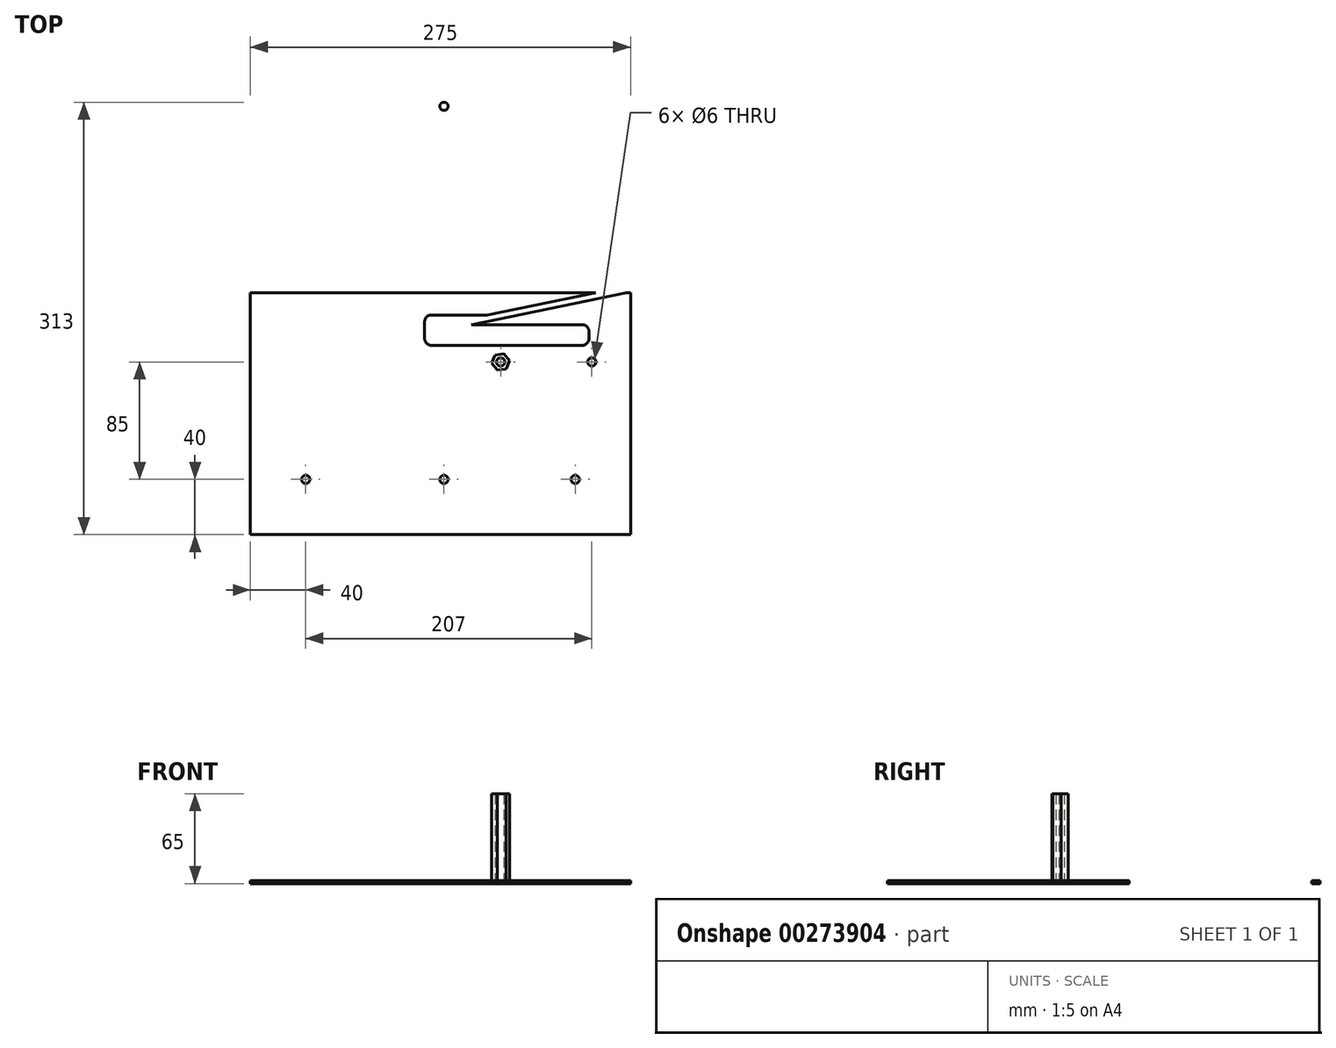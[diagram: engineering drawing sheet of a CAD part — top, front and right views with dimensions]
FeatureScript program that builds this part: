
annotation { "Feature Type Name" : "Feature", "Feature Type Description" : "" }
export const myFeature = defineFeature(function(context is Context, id is Id, definition is map)
    precondition{}
    {
        {
            var Q0;
            Q0=qCreatedBy(makeId("Top.planeOp"),FACE);
            var sketch = newSketch(context, id + "F0", { "sketchPlane" : qUnion([Q0])});
            skLineSegment(sketch, "E0.bottom", {"start": v(0, 0) * mm, "end": v(-275, 0) * mm});
            skLineSegment(sketch, "E0.top", {"start": v(-3, 175) * mm, "end": v(-275, 175) * mm});
            skLineSegment(sketch, "E0.left", {"start": v(0, 0) * mm, "end": v(0, 177) * mm});
            skLineSegment(sketch, "E0.right", {"start": v(-275, 0) * mm, "end": v(-275, 175) * mm});
            skLineSegment(sketch, "E1", {"start": v(-115, 152) * mm, "end": v(-35, 152) * mm});
            skLineSegment(sketch, "E2", {"start": v(-30, 147) * mm, "end": v(-30, 142) * mm});
            skLineSegment(sketch, "E3", {"start": v(-35, 137) * mm, "end": v(-144, 137) * mm});
            skLineSegment(sketch, "E4", {"start": v(-149, 142) * mm, "end": v(-149, 154) * mm});
            skLineSegment(sketch, "E5", {"start": v(-144, 159) * mm, "end": v(-104, 159) * mm});
            skLineSegment(sketch, "E6", {"start": v(-104, 159) * mm, "end": v(-25.36, 175) * mm});
            skCircle(sketch, "E7", {"center": v(-28, 125) * mm, "radius": 3 * mm});
            skCircle(sketch, "E8", {"center": v(-94, 125) * mm, "radius": 3 * mm});
            skPoint(sketch, "E9.visualSharp", {"position": v(0, 175) * mm});
            skLineSegment(sketch, "E10", {"start": v(-3, 175) * mm, "end": v(-115, 152) * mm});
            skLineSegment(sketch, "E11", {"start": v(-275, 40) * mm, "end": v(0, 40) * mm, "construction": true});
            skCircle(sketch, "E12", {"center": v(-235, 40) * mm, "radius": 3 * mm});
            skCircle(sketch, "E13", {"center": v(-135, 40) * mm, "radius": 3 * mm});
            skCircle(sketch, "E14", {"center": v(-40, 40) * mm, "radius": 3 * mm});
            skCircle(sketch, "E15.MirrorC", {"center": v(-135, 310) * mm, "radius": 3 * mm});
            skCircle(sketch, "E16.MirrorC", {"center": v(-94, 225) * mm, "radius": 3 * mm});
            skCircle(sketch, "E17.MirrorC", {"center": v(-40, 310) * mm, "radius": 3 * mm});
            skCircle(sketch, "E18.MirrorC", {"center": v(-28, 225) * mm, "radius": 3 * mm});
            skCircle(sketch, "E19.MirrorC", {"center": v(-235, 310) * mm, "radius": 3 * mm});
            skLineSegment(sketch, "E20.MirrorCS", {"start": v(-149, 208) * mm, "end": v(-149, 196) * mm});
            skLineSegment(sketch, "E21.MirrorCS", {"start": v(-144, 191) * mm, "end": v(-104, 191) * mm});
            skLineSegment(sketch, "E22.MirrorCS", {"start": v(-104, 191) * mm, "end": v(-25.36, 175) * mm});
            skLineSegment(sketch, "E23.MirrorCS", {"start": v(-35, 213) * mm, "end": v(-144, 213) * mm});
            skLineSegment(sketch, "E24.MirrorCS", {"start": v(-30, 203) * mm, "end": v(-30, 208) * mm});
            skLineSegment(sketch, "E25.MirrorCS", {"start": v(-115, 198) * mm, "end": v(-35, 198) * mm});
            skLineSegment(sketch, "E26.MirrorCS", {"start": v(-275, 350) * mm, "end": v(-275, 175) * mm});
            skLineSegment(sketch, "E27.MirrorCS", {"start": v(-3, 175) * mm, "end": v(-115, 198) * mm});
            skLineSegment(sketch, "E28.MirrorCS", {"start": v(0, 350) * mm, "end": v(0, 173) * mm});
            skLineSegment(sketch, "E29.MirrorCS", {"start": v(-275, 310) * mm, "end": v(0, 310) * mm, "construction": true});
            skLineSegment(sketch, "E30.MirrorCS", {"start": v(0, 350) * mm, "end": v(-275, 350) * mm});
            skCircle(sketch, "E31.cCircle", {"center": v(-94, 125) * mm, "radius": 5.57 * mm, "construction": true});
            skLineSegment(sketch, "E31.0", {"start": v(-91.54, 130.94) * mm, "end": v(-87.63, 125.85) * mm});
            skLineSegment(sketch, "E31.1", {"start": v(-87.63, 125.85) * mm, "end": v(-90.08, 119.9) * mm});
            skLineSegment(sketch, "E31.2", {"start": v(-90.08, 119.9) * mm, "end": v(-96.46, 119.06) * mm});
            skLineSegment(sketch, "E31.3", {"start": v(-96.46, 119.06) * mm, "end": v(-100.37, 124.15) * mm});
            skLineSegment(sketch, "E31.4", {"start": v(-100.37, 124.15) * mm, "end": v(-97.92, 130.1) * mm});
            skLineSegment(sketch, "E31.5", {"start": v(-97.92, 130.1) * mm, "end": v(-91.54, 130.94) * mm});
            skPoint(sketch, "E31.0.midPoint", {"position": v(-89.59, 128.4) * mm});
            skPoint(sketch, "E32.visualSharp", {"position": v(-149, 159) * mm});
            skArc(sketch, "E32.filletArc", {"start": v(-144, 159) * mm, "mid": v(-147.54, 157.54) * mm, "end": v(-149, 154) * mm});
            skPoint(sketch, "E33.visualSharp", {"position": v(-149, 137) * mm});
            skArc(sketch, "E33.filletArc", {"start": v(-149, 142) * mm, "mid": v(-147.54, 138.46) * mm, "end": v(-144, 137) * mm});
            skPoint(sketch, "E34.visualSharp", {"position": v(-30, 137) * mm});
            skArc(sketch, "E34.filletArc", {"start": v(-35, 137) * mm, "mid": v(-31.46, 138.46) * mm, "end": v(-30, 142) * mm});
            skPoint(sketch, "E35.visualSharp", {"position": v(-30, 152) * mm});
            skArc(sketch, "E35.filletArc", {"start": v(-30, 147) * mm, "mid": v(-31.46, 150.54) * mm, "end": v(-35, 152) * mm});
            skPoint(sketch, "E36.visualSharp", {"position": v(-149, 213) * mm});
            skArc(sketch, "E36.filletArc", {"start": v(-144, 213) * mm, "mid": v(-147.54, 211.54) * mm, "end": v(-149, 208) * mm});
            skPoint(sketch, "E37.visualSharp", {"position": v(-149, 191) * mm});
            skArc(sketch, "E37.filletArc", {"start": v(-149, 196) * mm, "mid": v(-147.54, 192.46) * mm, "end": v(-144, 191) * mm});
            skPoint(sketch, "E38.visualSharp", {"position": v(-30, 213) * mm});
            skArc(sketch, "E38.filletArc", {"start": v(-30, 208) * mm, "mid": v(-31.46, 211.54) * mm, "end": v(-35, 213) * mm});
            skPoint(sketch, "E39.visualSharp", {"position": v(-30, 198) * mm});
            skArc(sketch, "E39.filletArc", {"start": v(-35, 198) * mm, "mid": v(-31.46, 199.46) * mm, "end": v(-30, 203) * mm});
            skLineSegment(sketch, "E40", {"start": v(-3, 175) * mm, "end": v(0, 175) * mm});
            skLineSegment(sketch, "E41", {"start": v(0, 175) * mm, "end": v(0, 177) * mm});
            skLineSegment(sketch, "E42", {"start": v(0, 175) * mm, "end": v(-3, 175) * mm});
            skLineSegment(sketch, "E43", {"start": v(0, 175) * mm, "end": v(0, 173) * mm});
            skLineSegment(sketch, "E44", {"start": v(0, 175) * mm, "end": v(28, 175) * mm});
            skLineSegment(sketch, "E45", {"start": v(28, 175) * mm, "end": v(0, 150) * mm});
            skLineSegment(sketch, "E46.MirrorCS", {"start": v(28, 175) * mm, "end": v(0, 200) * mm});
            skSolve(sketch);
        }
        {
            var Q0;
            {var subQ4=sQuery(id+"F0.wireOp",EDGE,"E0.bottom");Q0=makeQuery(id+"F0.imprint","IMPRINT",FACE,{"disambiguationData":[TD([[makeQuery(id+"F0.imprint","IMPRINT",EDGE,{"derivedFrom":subQ4}),-1.0]])]});}
            var Q1;
            {var subQ0=sQuery(id+"F0.wireOp",EDGE,"E43");Q1=makeQuery(id+"F0.imprint","IMPRINT",FACE,{"disambiguationData":[TD([[makeQuery(id+"F0.imprint","IMPRINT",EDGE,{"derivedFrom":subQ0}),1.0]])]});}
            var Q2;
            Q2=makeQuery(id+"F0.imprint","IMPRINT",FACE,{"disambiguationData":[TD([[makeQuery(id+"F0.imprint","IMPRINT",EDGE,{"derivedFrom":sQuery(id+"F0.wireOp",EDGE,"E8")}),-1.0]])]});
            extrude(context, id + "F1", {"entities" : qUnion([Q0, Q1, Q2]), "depth" : 2 * mm});
        }
        {
            var Q0;
            Q0=makeQuery(id+"F0.imprint","IMPRINT",FACE,{"disambiguationData":[TD([[makeQuery(id+"F0.imprint","IMPRINT",EDGE,{"derivedFrom":sQuery(id+"F0.wireOp",EDGE,"E15.MirrorC")}),1.0]])]});
            var Q1;
            {var subQ0=sQuery(id+"F0.wireOp",EDGE,"E41");Q1=makeQuery(id+"F0.imprint","IMPRINT",FACE,{"disambiguationData":[TD([[makeQuery(id+"F0.imprint","IMPRINT",EDGE,{"derivedFrom":subQ0}),-1.0]])]});}
            extrude(context, id + "F2", {"entities" : qUnion([Q0, Q1]), "depth" : 2 * mm});
        }
        {
            var Q0;
            Q0=makeQuery(id+"F0.imprint","IMPRINT",FACE,{"disambiguationData":[TD([[makeQuery(id+"F0.imprint","IMPRINT",EDGE,{"derivedFrom":sQuery(id+"F0.wireOp",EDGE,"E8")}),-1.0]])]});
            extrude(context, id + "F3", {"entities" : qUnion([Q0]), "depth" : 65 * mm});
        }
    });
